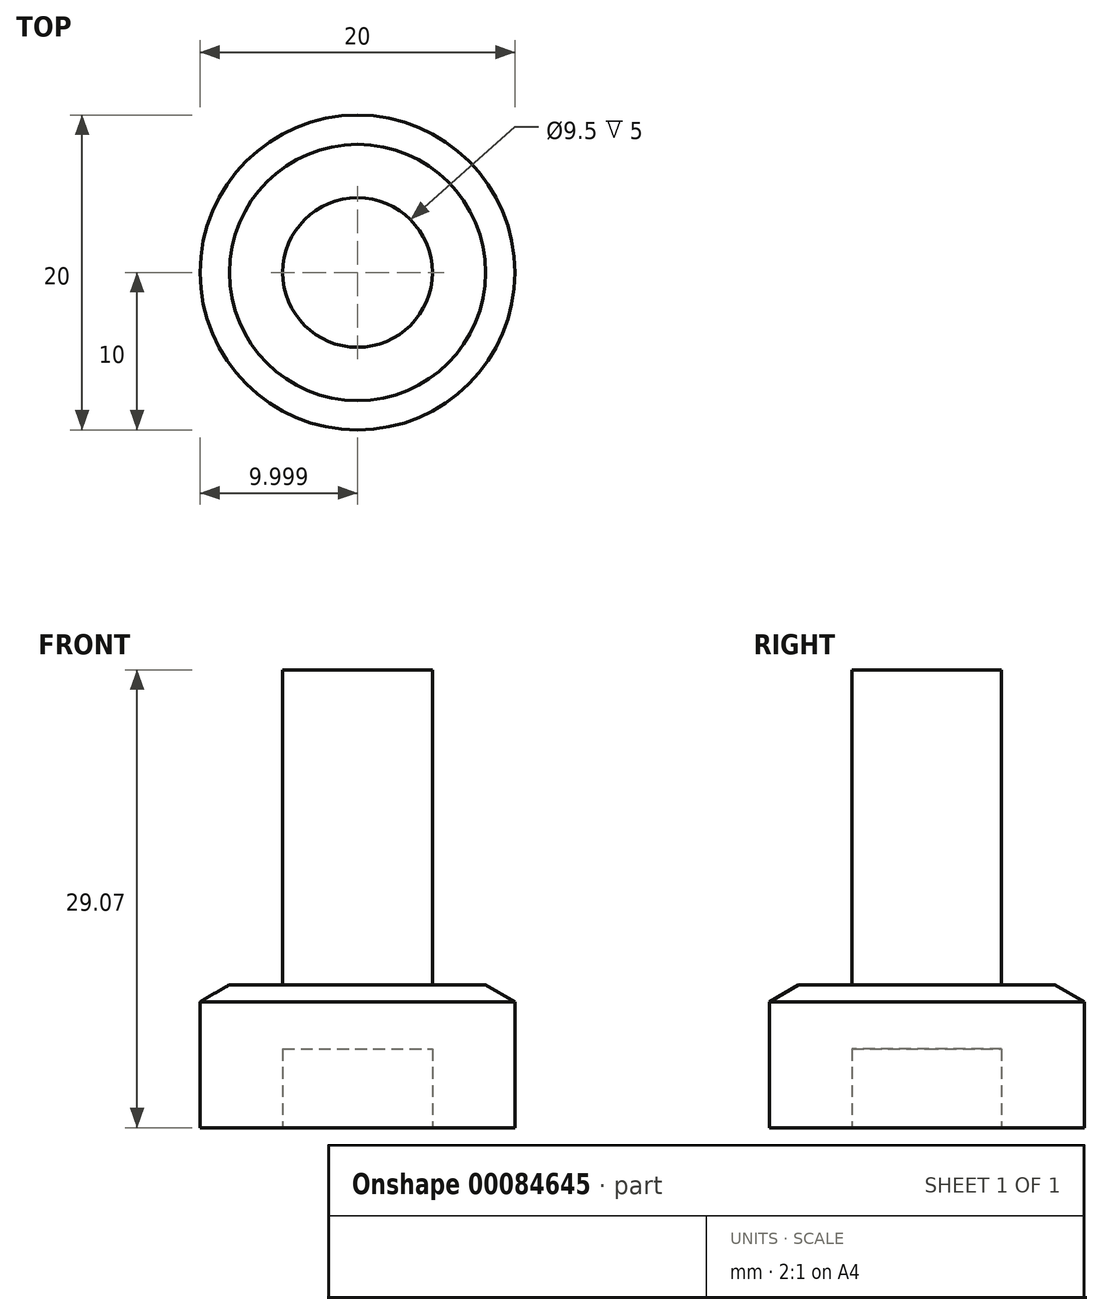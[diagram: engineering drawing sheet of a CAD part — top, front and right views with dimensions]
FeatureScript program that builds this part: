
annotation { "Feature Type Name" : "Feature", "Feature Type Description" : "" }
export const myFeature = defineFeature(function(context is Context, id is Id, definition is map)
    precondition{}
    {
        {
            var Q0;
            Q0=qCreatedBy(makeId("Front.planeOp"),FACE);
            var sketch = newSketch(context, id + "F0", { "sketchPlane" : qUnion([Q0])});
            skLineSegment(sketch, "E0.bottom", {"start": v(-30.55, 8) * mm, "end": v(-20.55, 8) * mm});
            skLineSegment(sketch, "E0.top", {"start": v(-30.55, 0) * mm, "end": v(-25.3, 0) * mm});
            skLineSegment(sketch, "E0.left", {"start": v(-30.55, 8) * mm, "end": v(-30.55, 0) * mm});
            skPoint(sketch, "E1", {"position": v(-20.55, 8) * mm});
            skPoint(sketch, "E2", {"position": v(-20.55, 0) * mm});
            skPoint(sketch, "E3", {"position": v(-20.55, 9.07) * mm});
            skLineSegment(sketch, "E4", {"start": v(-20.55, 8) * mm, "end": v(-20.55, 9.07) * mm});
            skLineSegment(sketch, "E5", {"start": v(-30.55, 8) * mm, "end": v(-28.7, 9.07) * mm});
            skLineSegment(sketch, "E6", {"start": v(-28.7, 9.07) * mm, "end": v(-20.55, 9.07) * mm});
            skLineSegment(sketch, "E7", {"start": v(-20.55, 8) * mm, "end": v(-20.55, 5) * mm});
            skPoint(sketch, "E0.right.end.orphan", {"position": v(-10.55, 0) * mm});
            skPoint(sketch, "E8.start.orphan", {"position": v(-10.55, 8) * mm});
            skLineSegment(sketch, "E9", {"start": v(-20.55, 9.07) * mm, "end": v(-20.55, 29.07) * mm});
            skLineSegment(sketch, "E10", {"start": v(-20.55, 29.07) * mm, "end": v(-25.3, 29.07) * mm});
            skLineSegment(sketch, "E11", {"start": v(-25.3, 29.07) * mm, "end": v(-25.3, 0) * mm});
            skPoint(sketch, "E12.start.orphan", {"position": v(-20.55, 4) * mm});
            skLineSegment(sketch, "E13", {"start": v(-20.55, 5) * mm, "end": v(-25.3, 5) * mm});
            skPoint(sketch, "E14", {"position": v(-20.55, 5) * mm});
            skSolve(sketch);
        }
        {
            var Q0;
            {var subQ0=sQuery(id+"F0.wireOp",EDGE,"E9");Q0=makeQuery(id+"F0.imprint","IMPRINT",FACE,{"disambiguationData":[TD([[makeQuery(id+"F0.imprint","IMPRINT",EDGE,{"derivedFrom":subQ0}),1.0]])]});}
            var Q1;
            {var subQ5=sQuery(id+"F0.wireOp",EDGE,"E0.top");Q1=makeQuery(id+"F0.imprint","IMPRINT",FACE,{"disambiguationData":[TD([[makeQuery(id+"F0.imprint","IMPRINT",EDGE,{"derivedFrom":subQ5}),1.0]])]});}
            var Q2;
            {var subQ0=sQuery(id+"F0.wireOp",EDGE,"E5");Q2=makeQuery(id+"F0.imprint","IMPRINT",FACE,{"disambiguationData":[TD([[makeQuery(id+"F0.imprint","IMPRINT",EDGE,{"derivedFrom":subQ0}),-1.0]])]});}
            var Q3;
            {var subQ0=sQuery(id+"F0.wireOp",EDGE,"E7");Q3=makeQuery(id+"F0.imprint","IMPRINT",FACE,{"disambiguationData":[TD([[makeQuery(id+"F0.imprint","IMPRINT",EDGE,{"derivedFrom":subQ0}),-1.0]])]});}
            var Q4;
            {var subQ0=sQuery(id+"F0.wireOp",EDGE,"E4");Q4=makeQuery(id+"F0.imprint","IMPRINT",FACE,{"disambiguationData":[TD([[makeQuery(id+"F0.imprint","IMPRINT",EDGE,{"derivedFrom":subQ0}),1.0]])]});}
            var Q5;
            Q5=sQuery(id+"F0.wireOp",EDGE,"E9");
            revolve(context, id + "F1", {"entities" : qUnion([Q0, Q1, Q2, Q3, Q4]), "axis" : qUnion([Q5]), "revolveType" : RevolveType.FULL});
        }
    });
